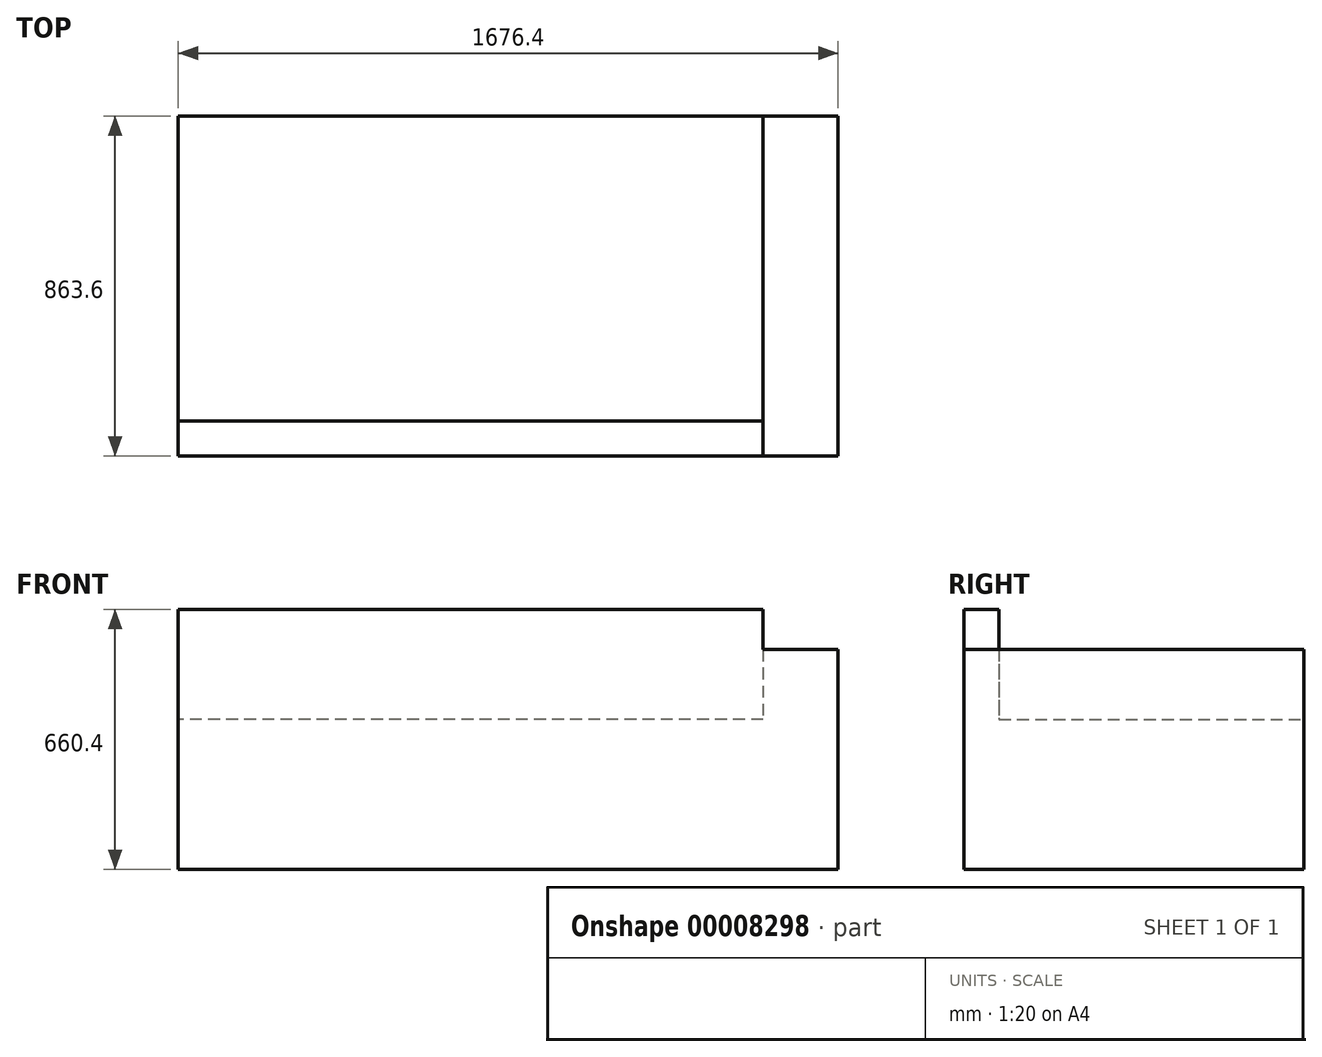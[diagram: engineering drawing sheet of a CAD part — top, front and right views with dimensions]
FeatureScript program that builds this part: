
annotation { "Feature Type Name" : "Feature", "Feature Type Description" : "" }
export const myFeature = defineFeature(function(context is Context, id is Id, definition is map)
    precondition{}
    {
        {
            var Q0;
            Q0=qCreatedBy(makeId("Top.planeOp"),FACE);
            var sketch = newSketch(context, id + "F0", { "sketchPlane" : qUnion([Q0])});
            skLineSegment(sketch, "E0.bottom", {"start": v(-822.43, 513.83) * mm, "end": v(853.97, 513.83) * mm});
            skLineSegment(sketch, "E0.top", {"start": v(-822.43, -349.77) * mm, "end": v(853.97, -349.77) * mm});
            skLineSegment(sketch, "E0.left", {"start": v(-822.43, 513.83) * mm, "end": v(-822.43, -349.77) * mm});
            skLineSegment(sketch, "E0.right", {"start": v(853.97, 513.83) * mm, "end": v(853.97, -349.77) * mm});
            skSolve(sketch);
        }
        {
            var Q0;
            Q0=makeQuery(id+"F0.imprint","IMPRINT",FACE,{"disambiguationData":[TD([[makeQuery(id+"F0.imprint","IMPRINT",EDGE,{"derivedFrom":sQuery(id+"F0.wireOp",EDGE,"E0.bottom")}),-1.0]])]});
            extrude(context, id + "F1", {"entities" : qUnion([Q0]), "depth" : 381 * mm});
        }
        {
            var Q0;
            Q0=makeQuery(id+"F1.opExtrude","CAP_FACE",FACE,{"disambiguationData":[OSD([sQuery(id+"F0.wireOp",EDGE,"E0.bottom"),sQuery(id+"F0.wireOp",EDGE,"E0.top"),sQuery(id+"F0.wireOp",EDGE,"E0.left"),sQuery(id+"F0.wireOp",EDGE,"E0.right")])],"isStart":false});
            var sketch = newSketch(context, id + "F2", { "sketchPlane" : qUnion([Q0])});
            skLineSegment(sketch, "E1.bottom", {"start": v(853.97, -349.77) * mm, "end": v(663.47, -349.77) * mm});
            skLineSegment(sketch, "E1.top", {"start": v(853.97, 513.83) * mm, "end": v(663.47, 513.83) * mm});
            skLineSegment(sketch, "E1.left", {"start": v(853.97, -349.77) * mm, "end": v(853.97, 513.83) * mm});
            skLineSegment(sketch, "E1.right", {"start": v(663.47, -349.77) * mm, "end": v(663.47, 513.83) * mm});
            skSolve(sketch);
        }
        {
            var Q0;
            Q0=makeQuery(id+"F2.imprint","IMPRINT",FACE,{"disambiguationData":[TD([[makeQuery(id+"F2.imprint","IMPRINT",EDGE,{"derivedFrom":sQuery(id+"F2.wireOp",EDGE,"E1.bottom")}),1.0]])]});
            extrude(context, id + "F3", {"entities" : qUnion([Q0]), "operationType" : NewBodyOperationType.ADD, "depth" : 177.8 * mm});
        }
        {
            var Q0;
            Q0=makeQuery(id+"F1.opExtrude","CAP_FACE",FACE,{"disambiguationData":[OSD([sQuery(id+"F0.wireOp",EDGE,"E0.bottom"),sQuery(id+"F0.wireOp",EDGE,"E0.top"),sQuery(id+"F0.wireOp",EDGE,"E0.left"),sQuery(id+"F0.wireOp",EDGE,"E0.right")])],"isStart":false});
            var sketch = newSketch(context, id + "F4", { "sketchPlane" : qUnion([Q0])});
            skLineSegment(sketch, "E2.bottom", {"start": v(663.47, -349.77) * mm, "end": v(-822.43, -349.77) * mm});
            skLineSegment(sketch, "E2.top", {"start": v(663.47, -260.87) * mm, "end": v(-822.43, -260.87) * mm});
            skLineSegment(sketch, "E2.left", {"start": v(663.47, -349.77) * mm, "end": v(663.47, -260.87) * mm});
            skLineSegment(sketch, "E2.right", {"start": v(-822.43, -349.77) * mm, "end": v(-822.43, -260.87) * mm});
            skSolve(sketch);
        }
        {
            var Q0;
            Q0=makeQuery(id+"F4.imprint","IMPRINT",FACE,{"disambiguationData":[TD([[makeQuery(id+"F4.imprint","IMPRINT",EDGE,{"derivedFrom":sQuery(id+"F4.wireOp",EDGE,"E2.bottom")}),1.0]])]});
            extrude(context, id + "F5", {"entities" : qUnion([Q0]), "operationType" : NewBodyOperationType.ADD, "depth" : 279.4 * mm});
        }
    });
